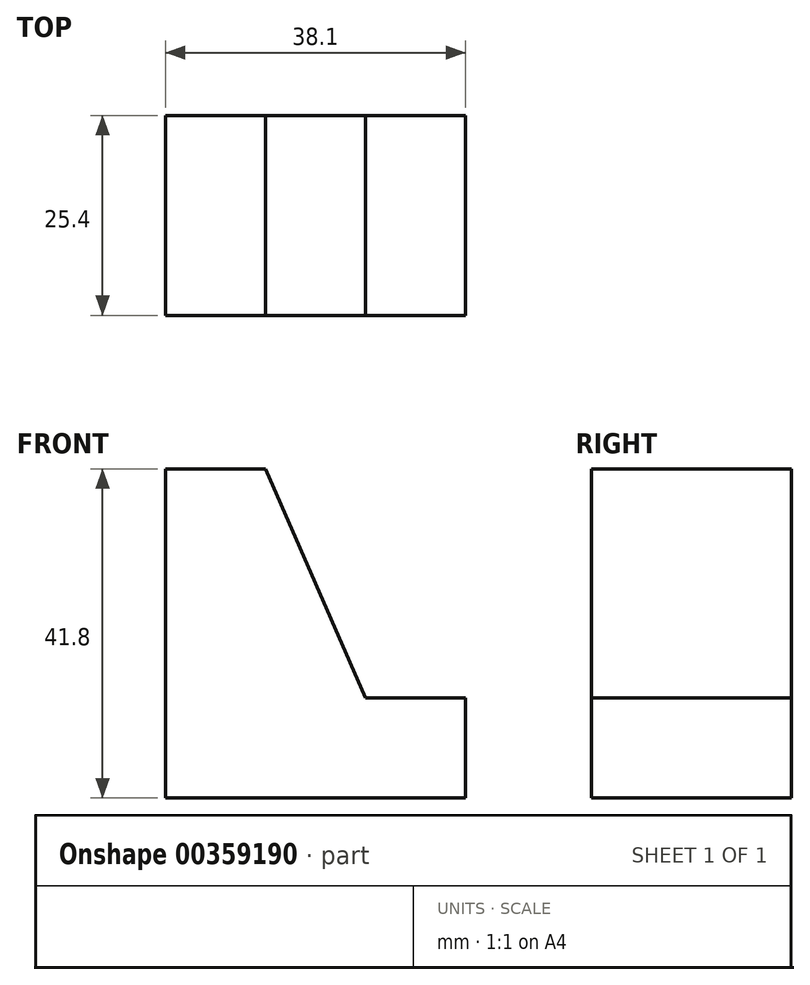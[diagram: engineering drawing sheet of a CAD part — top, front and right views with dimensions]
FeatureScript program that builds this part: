
annotation { "Feature Type Name" : "Feature", "Feature Type Description" : "" }
export const myFeature = defineFeature(function(context is Context, id is Id, definition is map)
    precondition{}
    {
        {
            var Q0;
            Q0=qCreatedBy(makeId("Front.planeOp"),FACE);
            var sketch = newSketch(context, id + "F0", { "sketchPlane" : qUnion([Q0])});
            skLineSegment(sketch, "E0", {"start": v(0, 41.8) * mm, "end": v(0, 0) * mm});
            skLineSegment(sketch, "E1", {"start": v(0, 0) * mm, "end": v(38.1, 0) * mm});
            skLineSegment(sketch, "E2", {"start": v(38.1, 0) * mm, "end": v(38.1, 12.7) * mm});
            skLineSegment(sketch, "E3", {"start": v(38.1, 12.7) * mm, "end": v(25.4, 12.7) * mm});
            skLineSegment(sketch, "E4", {"start": v(0, 41.8) * mm, "end": v(12.7, 41.8) * mm});
            skLineSegment(sketch, "E5", {"start": v(12.7, 41.8) * mm, "end": v(25.4, 12.7) * mm});
            skSolve(sketch);
        }
        {
            var Q0;
            Q0 = qSketchRegion(id + "F0", true);
            extrude(context, id + "F1", {"entities" : qUnion([Q0]), "depth" : 25.4 * mm});
        }
    });
